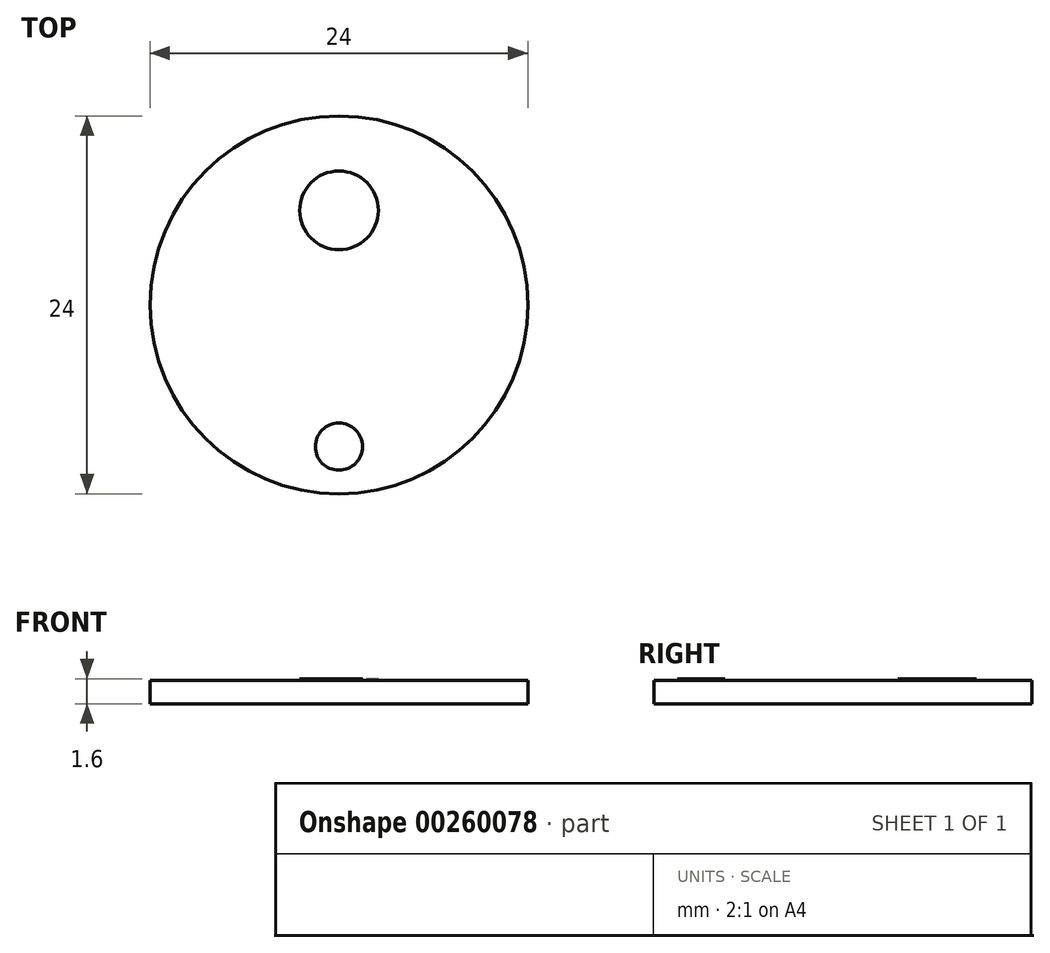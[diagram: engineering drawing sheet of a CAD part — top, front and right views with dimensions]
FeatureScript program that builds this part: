
annotation { "Feature Type Name" : "Feature", "Feature Type Description" : "" }
export const myFeature = defineFeature(function(context is Context, id is Id, definition is map)
    precondition{}
    {
        {
            var Q0;
            Q0=qCreatedBy(makeId("Top.planeOp"),FACE);
            var sketch = newSketch(context, id + "F0", { "sketchPlane" : qUnion([Q0])});
            skCircle(sketch, "E0", {"center": v(0, 0) * mm, "radius": 12 * mm});
            skSolve(sketch);
        }
        {
            var Q0;
            Q0 = qSketchRegion(id + "F0", true);
            extrude(context, id + "F1", {"entities" : qUnion([Q0]), "depth" : 1.5 * mm});
        }
        {
            var Q0;
            Q0=makeQuery(id+"F1.opExtrude","CAP_FACE",FACE,{"disambiguationData":[OSD([sQuery(id+"F0.wireOp",EDGE,"E0")])],"isStart":false});
            var sketch = newSketch(context, id + "F2", { "sketchPlane" : qUnion([Q0])});
            skLineSegment(sketch, "E1", {"start": v(0, 0) * mm, "end": v(0, 6) * mm, "construction": true});
            skCircle(sketch, "E2", {"center": v(0, 6) * mm, "radius": 2.5 * mm});
            skLineSegment(sketch, "E3", {"start": v(0, 0) * mm, "end": v(0, -9) * mm, "construction": true});
            skCircle(sketch, "E4", {"center": v(0, -9) * mm, "radius": 1.5 * mm});
            skSolve(sketch);
        }
        {
            var Q0;
            Q0=makeQuery(id+"F2.imprint","IMPRINT",FACE,{"disambiguationData":[TD([[makeQuery(id+"F2.imprint","IMPRINT",EDGE,{"derivedFrom":sQuery(id+"F2.wireOp",EDGE,"E2")}),1.0]])]});
            var Q1;
            Q1=makeQuery(id+"F2.imprint","IMPRINT",FACE,{"disambiguationData":[TD([[makeQuery(id+"F2.imprint","IMPRINT",EDGE,{"derivedFrom":sQuery(id+"F2.wireOp",EDGE,"E4")}),1.0]])]});
            extrude(context, id + "F3", {"entities" : qUnion([Q0, Q1]), "operationType" : NewBodyOperationType.ADD, "depth" : 0.1 * mm});
        }
    });
